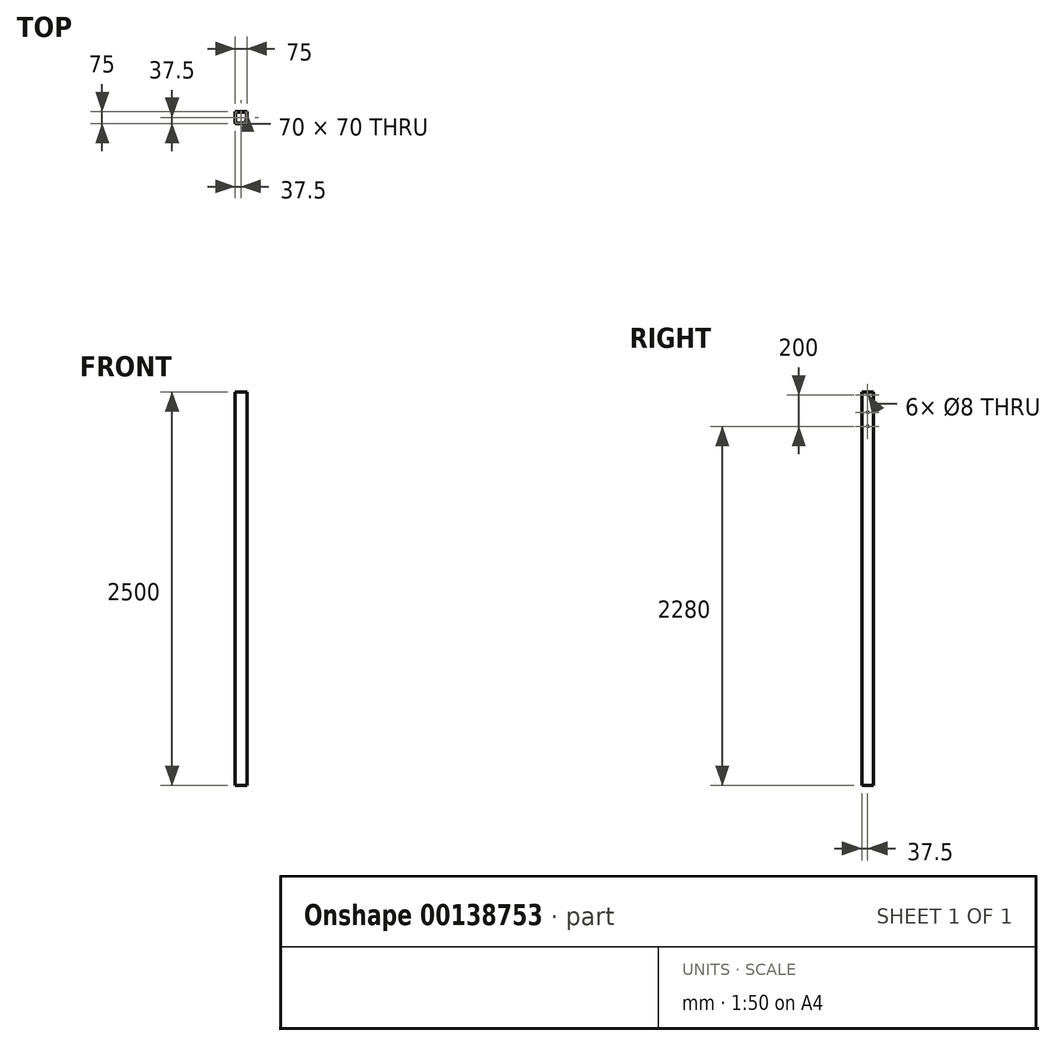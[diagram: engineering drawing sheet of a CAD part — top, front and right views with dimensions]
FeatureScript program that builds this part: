
annotation { "Feature Type Name" : "Feature", "Feature Type Description" : "" }
export const myFeature = defineFeature(function(context is Context, id is Id, definition is map)
    precondition{}
    {
        {
            var Q0;
            Q0=qCreatedBy(makeId("Top.planeOp"),FACE);
            var sketch = newSketch(context, id + "F0", { "sketchPlane" : qUnion([Q0])});
            skLineSegment(sketch, "E0.bottom", {"start": v(-37.5, 37.5) * mm, "end": v(37.5, 37.5) * mm});
            skLineSegment(sketch, "E0.top", {"start": v(-37.5, -37.5) * mm, "end": v(37.5, -37.5) * mm});
            skLineSegment(sketch, "E0.left", {"start": v(-37.5, 37.5) * mm, "end": v(-37.5, -37.5) * mm});
            skLineSegment(sketch, "E0.right", {"start": v(37.5, 37.5) * mm, "end": v(37.5, -37.5) * mm});
            skLineSegment(sketch, "E1.bottom", {"start": v(-35, 35) * mm, "end": v(35, 35) * mm});
            skLineSegment(sketch, "E1.top", {"start": v(-35, -35) * mm, "end": v(35, -35) * mm});
            skLineSegment(sketch, "E1.left", {"start": v(-35, 35) * mm, "end": v(-35, -35) * mm});
            skLineSegment(sketch, "E1.right", {"start": v(35, 35) * mm, "end": v(35, -35) * mm});
            skSolve(sketch);
        }
        {
            var Q0;
            Q0=qSketchRegion(id+"F0",true);
            extrude(context, id + "F1", {"entities" : qUnion([Q0]), "endBound" : BoundingType.SYMMETRIC, "depth" : 2500 * mm});
        }
        {
            var Q0;
            Q0=qCreatedBy(makeId("Right.planeOp"),FACE);
            var sketch = newSketch(context, id + "F2", { "sketchPlane" : qUnion([Q0])});
            skCircle(sketch, "E2", {"center": v(0, 1230) * mm, "radius": 4 * mm});
            skCircle(sketch, "E3", {"center": v(0, 1120) * mm, "radius": 4 * mm});
            skCircle(sketch, "E4", {"center": v(0, 1030) * mm, "radius": 4 * mm});
            skSolve(sketch);
        }
        {
            var Q0;
            Q0=qSketchRegion(id+"F2",true);
            extrude(context, id + "F3", {"entities" : qUnion([Q0]), "operationType" : NewBodyOperationType.REMOVE, "endBound" : BoundingType.SYMMETRIC, "depth" : 76 * mm});
        }
    });
